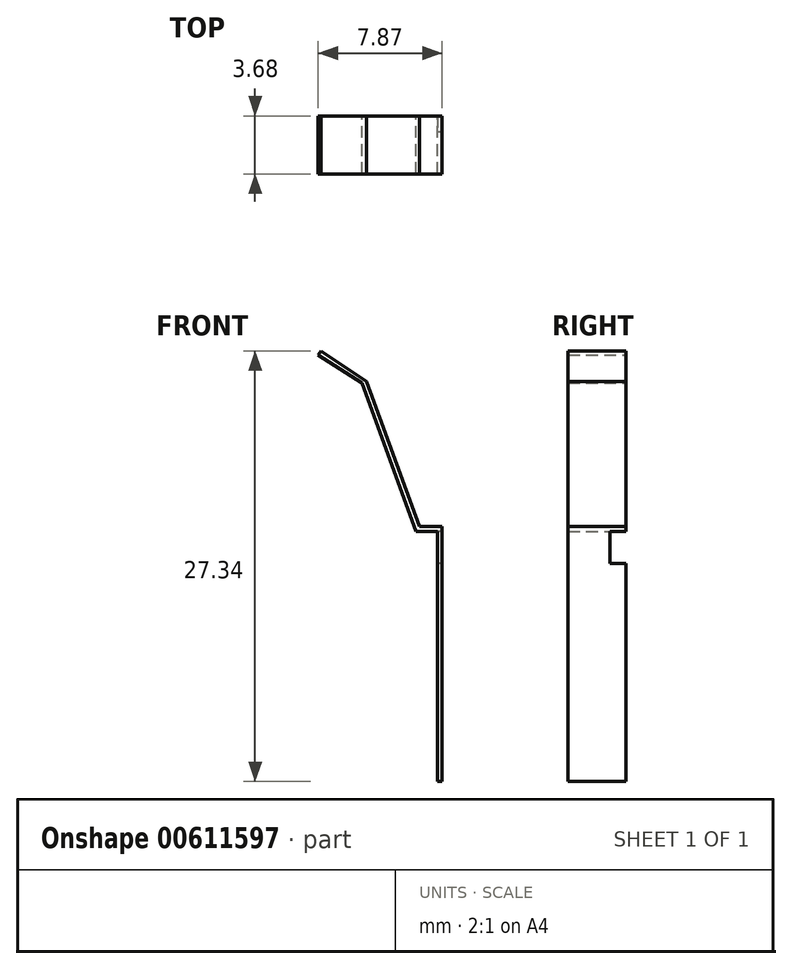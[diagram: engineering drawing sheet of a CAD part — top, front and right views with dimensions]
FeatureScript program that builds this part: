
annotation { "Feature Type Name" : "Feature", "Feature Type Description" : "" }
export const myFeature = defineFeature(function(context is Context, id is Id, definition is map)
    precondition{}
    {
        {
            var Q0;
            Q0=qCreatedBy(makeId("Front.planeOp"),FACE);
            var sketch = newSketch(context, id + "F0", { "sketchPlane" : qUnion([Q0])});
            skLineSegment(sketch, "E0.bottom", {"start": v(0, -15.88) * mm, "end": v(0.3, -15.88) * mm});
            skLineSegment(sketch, "E0.left", {"start": v(0, -15.88) * mm, "end": v(0, 0) * mm});
            skLineSegment(sketch, "E0.right", {"start": v(0.3, -15.88) * mm, "end": v(0.3, 0) * mm});
            skLineSegment(sketch, "E1.bottom", {"start": v(0, 0) * mm, "end": v(-1.35, 0) * mm});
            skLineSegment(sketch, "E1.top", {"start": v(0.3, 0.3) * mm, "end": v(-1.13, 0.3) * mm});
            skLineSegment(sketch, "E1.left", {"start": v(0.3, 0) * mm, "end": v(0.3, 0.3) * mm});
            skLineSegment(sketch, "E2", {"start": v(-1.35, 0) * mm, "end": v(-4.78, 9.43) * mm});
            skLineSegment(sketch, "E3", {"start": v(-4.49, 9.53) * mm, "end": v(-1.13, 0.3) * mm});
            skLineSegment(sketch, "E4", {"start": v(-4.78, 9.43) * mm, "end": v(-7.57, 11.2) * mm});
            skLineSegment(sketch, "E5", {"start": v(-7.57, 11.2) * mm, "end": v(-7.4, 11.46) * mm});
            skLineSegment(sketch, "E6", {"start": v(-7.4, 11.46) * mm, "end": v(-4.49, 9.53) * mm});
            skSolve(sketch);
        }
        {
            var Q0;
            Q0=makeQuery(id+"F0.imprint","IMPRINT",FACE,{"disambiguationData":[TD([[makeQuery(id+"F0.imprint","IMPRINT",EDGE,{"derivedFrom":sQuery(id+"F0.wireOp",EDGE,"E0.bottom")}),1.0]])]});
            extrude(context, id + "F1", {"entities" : qUnion([Q0]), "endBound" : BoundingType.SYMMETRIC, "depth" : 3.68 * mm, "offsetDistance" : 25.4 * mm});
        }
        {
            var Q0;
            Q0=makeQuery(id+"F1.opExtrude","SWEPT_FACE",FACE,{"disambiguationData":[OSD([sQuery(id+"F0.wireOp",EDGE,"E0.left")])]});
            var sketch = newSketch(context, id + "F2", { "sketchPlane" : qUnion([Q0])});
            skLineSegment(sketch, "E7.bottom", {"start": v(-1.84, 0) * mm, "end": v(-0.83, 0) * mm});
            skLineSegment(sketch, "E7.top", {"start": v(-1.84, -2.03) * mm, "end": v(-0.83, -2.03) * mm});
            skLineSegment(sketch, "E7.left", {"start": v(-1.84, 0) * mm, "end": v(-1.84, -2.03) * mm});
            skLineSegment(sketch, "E7.right", {"start": v(-0.83, 0) * mm, "end": v(-0.83, -2.03) * mm});
            skSolve(sketch);
        }
        {
            var Q0;
            Q0=makeQuery(id+"F2.imprint","IMPRINT",FACE,{"disambiguationData":[TD([[makeQuery(id+"F2.imprint","IMPRINT",EDGE,{"derivedFrom":sQuery(id+"F2.wireOp",EDGE,"E7.bottom")}),1.0]])]});
            extrude(context, id + "F3", {"entities" : qUnion([Q0]), "operationType" : NewBodyOperationType.REMOVE, "oppositeDirection" : true, "depth" : 25.4 * mm, "offsetDistance" : 25.4 * mm});
        }
    });
